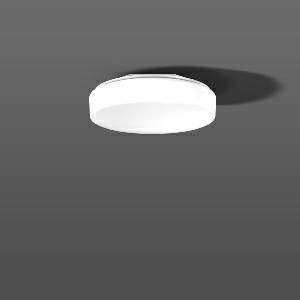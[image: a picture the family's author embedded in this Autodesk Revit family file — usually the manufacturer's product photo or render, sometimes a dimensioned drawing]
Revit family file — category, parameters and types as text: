
# Revit family: flat_polymero_kreis_672478_002_1_04_cdfb
name_source: partatom
category: Lighting Fixtures
units: mm (PartAtom-declared; Revit-internal decimal feet)

## family parameters
Cut with Voids When Loaded = No
Host = Face
Light Source = No
Part Type = Normal
Room Calculation Point = No
Round Connector Dimension = Use Diameter
Shared = No

## types (1)
- FLAT POLYMERO KREIS (1 x LED Modul 840, 1200 lm, 4000)
    Apparent Load = 13 VA
    CIE Flux Codes = 41 72 91 84 100
    Color Rendering = 80
    Color Temperature = 4000
    Default Elevation = 1800 mm
    Description = Series: FLAT POLYMERO KREIS
Decorative round surface-mounted luminaire. For escape route illumination. Base: metal, powder-coated. Diffuser made of non-yellowing plastic (PMMA), opal. Diffuser fastening: patented push system. Suitable for Ceiling mounting, Wall (surface). Self-contained system with automatic self-test and feedback to the RZB monitoring system MULTIDIGIT. 
Colour: white
Diameter: 360 mm
Height: 87 mm
Weight: 1.44 kg
Operating mode: Combined NL readiness
Duration time: 3 h
Lamp: LED
Socket: without socket
Colour temperature: 4000K
Colour rendering index (CRI): 80
System power: 13 W
Rated luminous flux: 1200 lm
Luminous flux, emergency: 170 lm
System power, emergency: -
Control gear: Converter not necessary
Protection class: I
Type of protection: IP 40
    Height = 87 mm
    Lamp = 1 x LED Modul 840
    Lamp Light Flux = 1200 lm
    Lamp count = 1
    Length = 360 mm
    Lifetime = 50000 h
    Luminous efficacy = 92 lm/W
    Manufacturer = RZB
    ModVariant = No
    Model = 672478.002.1.04
    Mounting Place = Ceiling, Wall
    Mounting Type = Surface mounted
    Number of Poles = 1
    OnlyDefault = Yes
    Power Factor = 1
    Product Name = FLAT POLYMERO KREIS
    Product group = Surface mounted ceiling and wall luminaires
    ProductGroupID = 305
    Protection Class = Protection class I
    Protection Degree = IP 40
    RLX_Detail_Level = 1
    RLX_Emergency_Light_Flux = 170 lm
    RLX_Emergency_Type = 3
    RLX_Emergency_Type_DB = Yes
    RlxData = <blob elided: 51993 chars, md5=b8e7fe2f>
    Socket = socket
    Standby Power = 0 W
    System Light Flux = 1200 lm
    System Power = 13 W
    Type Comments = Product without accessories
    Type Image = 672092.002.1.jpg
    URL = http://relux.com
    VarID = ---
    Voltage = 230 V
    Voltage Range = 220-240 V
    Weight = 0.00 kg
    Width = 0 mm  [stored 0 ft]

note: [stored X ft] marks values corroborated as IEEE doubles in the binary element streams (Revit-internal decimal feet)

## geometry (parser evidence)
native form markers: Blend x4, Sweep x14
no freeform markers — native parametric forms only
